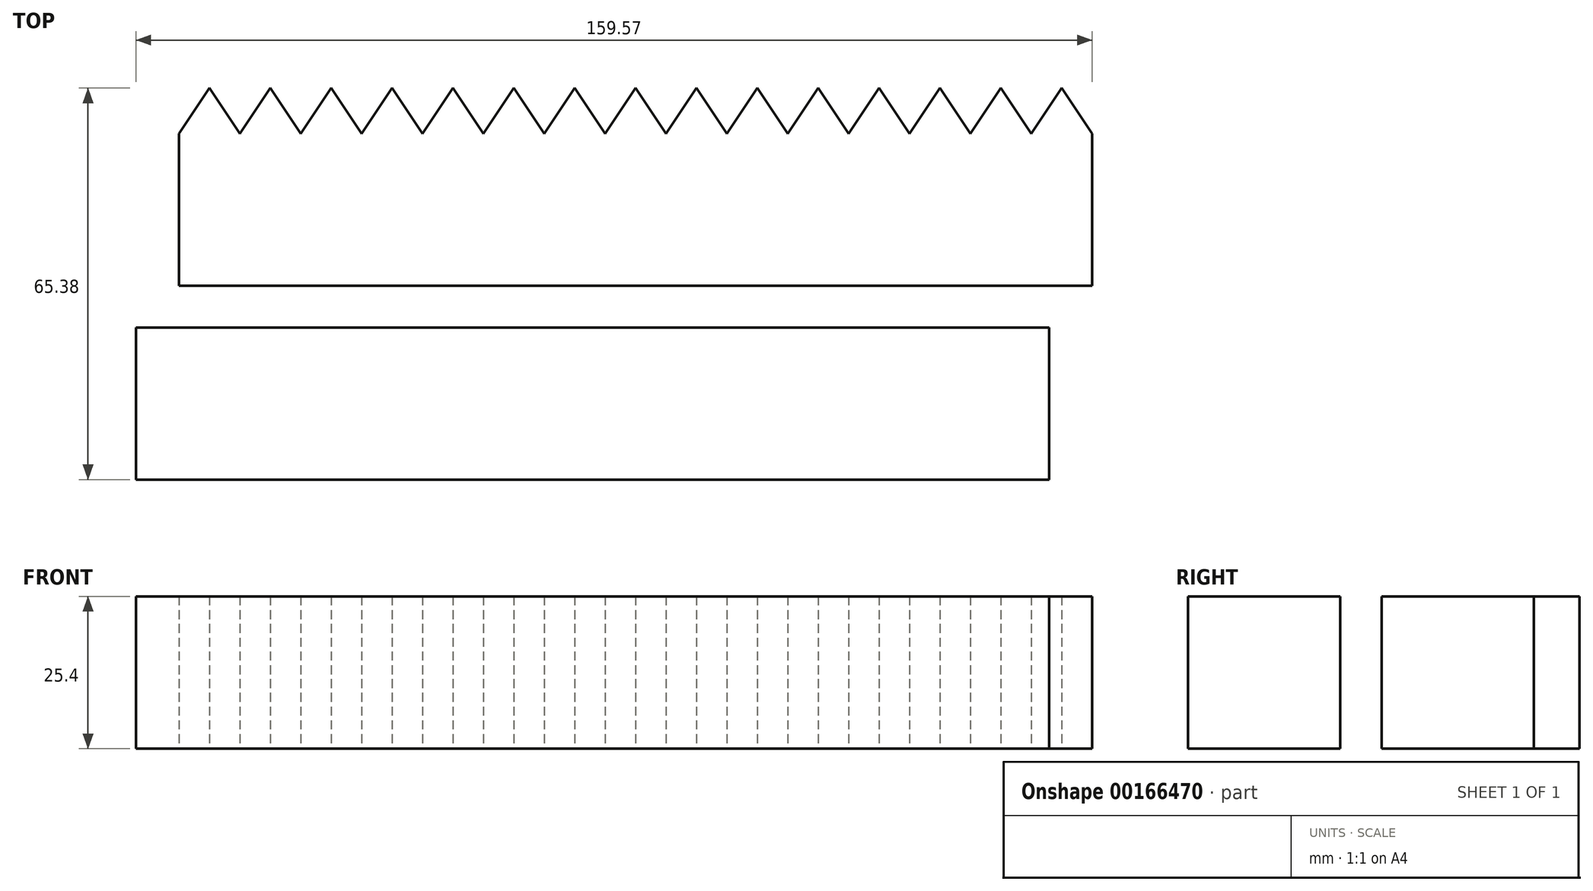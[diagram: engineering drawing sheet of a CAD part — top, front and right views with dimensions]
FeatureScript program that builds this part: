
annotation { "Feature Type Name" : "Feature", "Feature Type Description" : "" }
export const myFeature = defineFeature(function(context is Context, id is Id, definition is map)
    precondition{}
    {
        {
            var Q0;
            Q0=qCreatedBy(makeId("Top.planeOp"),FACE);
            var sketch = newSketch(context, id + "F0", { "sketchPlane" : qUnion([Q0])});
            skLineSegment(sketch, "E0.bottom", {"start": v(56.68, 12.19) * mm, "end": v(-95.72, 12.19) * mm});
            skLineSegment(sketch, "E0.top", {"start": v(56.68, -13.21) * mm, "end": v(-95.72, -13.21) * mm});
            skLineSegment(sketch, "E0.left", {"start": v(56.68, 12.19) * mm, "end": v(56.68, -13.21) * mm});
            skLineSegment(sketch, "E0.right", {"start": v(-95.72, 12.19) * mm, "end": v(-95.72, -13.21) * mm});
            skPoint(sketch, "E0.middle", {"position": v(-19.52, -0.51) * mm});
            skLineSegment(sketch, "E1", {"start": v(-90.64, 12.19) * mm, "end": v(-90.64, 19.8) * mm});
            skLineSegment(sketch, "E2", {"start": v(-90.64, 19.8) * mm, "end": v(-85.56, 12.19) * mm});
            skLineSegment(sketch, "E3", {"start": v(-85.56, 12.19) * mm, "end": v(-90.64, 19.8) * mm});
            skLineSegment(sketch, "E4", {"start": v(-95.72, 12.19) * mm, "end": v(-90.64, 19.8) * mm});
            skLineSegment(sketch, "E5.2.0.0", {"start": v(209.08, 12.19) * mm, "end": v(214.16, 19.8) * mm});
            skLineSegment(sketch, "E5.2.0.1", {"start": v(219.24, 12.19) * mm, "end": v(214.16, 19.8) * mm});
            skLineSegment(sketch, "E5.3.0.0", {"start": v(361.48, 12.19) * mm, "end": v(366.56, 19.8) * mm});
            skLineSegment(sketch, "E5.3.0.1", {"start": v(371.64, 12.19) * mm, "end": v(366.56, 19.8) * mm});
            skLineSegment(sketch, "E5.4.0.0", {"start": v(513.88, 12.19) * mm, "end": v(518.96, 19.8) * mm});
            skLineSegment(sketch, "E5.4.0.1", {"start": v(524.04, 12.19) * mm, "end": v(518.96, 19.8) * mm});
            skLineSegment(sketch, "E5.5.0.0", {"start": v(666.28, 12.19) * mm, "end": v(671.36, 19.8) * mm});
            skLineSegment(sketch, "E5.5.0.1", {"start": v(676.44, 12.19) * mm, "end": v(671.36, 19.8) * mm});
            skLineSegment(sketch, "E5.6.0.0", {"start": v(818.68, 12.19) * mm, "end": v(823.76, 19.8) * mm});
            skLineSegment(sketch, "E5.6.0.1", {"start": v(828.84, 12.19) * mm, "end": v(823.76, 19.8) * mm});
            skLineSegment(sketch, "E5.7.0.0", {"start": v(971.08, 12.19) * mm, "end": v(976.16, 19.8) * mm});
            skLineSegment(sketch, "E5.7.0.1", {"start": v(981.24, 12.19) * mm, "end": v(976.16, 19.8) * mm});
            skLineSegment(sketch, "E5.8.0.0", {"start": v(1123.48, 12.19) * mm, "end": v(1128.56, 19.8) * mm});
            skLineSegment(sketch, "E5.8.0.1", {"start": v(1133.64, 12.19) * mm, "end": v(1128.56, 19.8) * mm});
            skLineSegment(sketch, "E5.9.0.0", {"start": v(1275.88, 12.19) * mm, "end": v(1280.96, 19.8) * mm});
            skLineSegment(sketch, "E5.9.0.1", {"start": v(1286.04, 12.19) * mm, "end": v(1280.96, 19.8) * mm});
            skLineSegment(sketch, "E5.10.0.0", {"start": v(1428.28, 12.19) * mm, "end": v(1433.36, 19.8) * mm});
            skLineSegment(sketch, "E5.10.0.1", {"start": v(1438.44, 12.19) * mm, "end": v(1433.36, 19.8) * mm});
            skLineSegment(sketch, "E5.11.0.0", {"start": v(1580.68, 12.19) * mm, "end": v(1585.76, 19.8) * mm});
            skLineSegment(sketch, "E5.11.0.1", {"start": v(1590.84, 12.19) * mm, "end": v(1585.76, 19.8) * mm});
            skLineSegment(sketch, "E5.12.0.0", {"start": v(1733.08, 12.19) * mm, "end": v(1738.16, 19.8) * mm});
            skLineSegment(sketch, "E5.12.0.1", {"start": v(1743.24, 12.19) * mm, "end": v(1738.16, 19.8) * mm});
            skLineSegment(sketch, "E5.13.0.0", {"start": v(1885.48, 12.19) * mm, "end": v(1890.56, 19.8) * mm});
            skLineSegment(sketch, "E5.13.0.1", {"start": v(1895.64, 12.19) * mm, "end": v(1890.56, 19.8) * mm});
            skLineSegment(sketch, "E5.14.0.0", {"start": v(2037.88, 12.19) * mm, "end": v(2042.96, 19.8) * mm});
            skLineSegment(sketch, "E5.14.0.1", {"start": v(2048.04, 12.19) * mm, "end": v(2042.96, 19.8) * mm});
            skLineSegment(sketch, "E5.direction1", {"start": v(-95.72, 12.19) * mm, "end": v(56.68, 12.19) * mm, "construction": true});
            skLineSegment(sketch, "E6.1.0.0", {"start": v(-85.56, 12.19) * mm, "end": v(-80.48, 19.8) * mm});
            skLineSegment(sketch, "E6.1.0.1", {"start": v(-75.4, 12.19) * mm, "end": v(-80.48, 19.8) * mm});
            skLineSegment(sketch, "E6.2.0.0", {"start": v(-75.4, 12.19) * mm, "end": v(-70.32, 19.8) * mm});
            skLineSegment(sketch, "E6.2.0.1", {"start": v(-65.24, 12.19) * mm, "end": v(-70.32, 19.8) * mm});
            skLineSegment(sketch, "E6.3.0.0", {"start": v(-65.24, 12.19) * mm, "end": v(-60.16, 19.8) * mm});
            skLineSegment(sketch, "E6.3.0.1", {"start": v(-55.08, 12.19) * mm, "end": v(-60.16, 19.8) * mm});
            skLineSegment(sketch, "E6.4.0.0", {"start": v(-55.08, 12.19) * mm, "end": v(-50, 19.8) * mm});
            skLineSegment(sketch, "E6.4.0.1", {"start": v(-44.92, 12.19) * mm, "end": v(-50, 19.8) * mm});
            skLineSegment(sketch, "E6.5.0.0", {"start": v(-44.92, 12.19) * mm, "end": v(-39.84, 19.8) * mm});
            skLineSegment(sketch, "E6.5.0.1", {"start": v(-34.76, 12.19) * mm, "end": v(-39.84, 19.8) * mm});
            skLineSegment(sketch, "E6.6.0.0", {"start": v(-34.76, 12.19) * mm, "end": v(-29.68, 19.8) * mm});
            skLineSegment(sketch, "E6.6.0.1", {"start": v(-24.6, 12.19) * mm, "end": v(-29.68, 19.8) * mm});
            skLineSegment(sketch, "E6.7.0.0", {"start": v(-24.6, 12.19) * mm, "end": v(-19.52, 19.8) * mm});
            skLineSegment(sketch, "E6.7.0.1", {"start": v(-14.44, 12.19) * mm, "end": v(-19.52, 19.8) * mm});
            skLineSegment(sketch, "E6.8.0.0", {"start": v(-14.44, 12.19) * mm, "end": v(-9.36, 19.8) * mm});
            skLineSegment(sketch, "E6.8.0.1", {"start": v(-4.28, 12.19) * mm, "end": v(-9.36, 19.8) * mm});
            skLineSegment(sketch, "E6.9.0.0", {"start": v(-4.28, 12.19) * mm, "end": v(0.8, 19.8) * mm});
            skLineSegment(sketch, "E6.9.0.1", {"start": v(5.88, 12.19) * mm, "end": v(0.8, 19.8) * mm});
            skLineSegment(sketch, "E6.10.0.0", {"start": v(5.88, 12.19) * mm, "end": v(10.96, 19.8) * mm});
            skLineSegment(sketch, "E6.10.0.1", {"start": v(16.04, 12.19) * mm, "end": v(10.96, 19.8) * mm});
            skLineSegment(sketch, "E6.11.0.0", {"start": v(16.04, 12.19) * mm, "end": v(21.12, 19.8) * mm});
            skLineSegment(sketch, "E6.11.0.1", {"start": v(26.2, 12.19) * mm, "end": v(21.12, 19.8) * mm});
            skLineSegment(sketch, "E6.12.0.0", {"start": v(26.2, 12.19) * mm, "end": v(31.28, 19.8) * mm});
            skLineSegment(sketch, "E6.12.0.1", {"start": v(36.36, 12.19) * mm, "end": v(31.28, 19.8) * mm});
            skLineSegment(sketch, "E6.13.0.0", {"start": v(36.36, 12.19) * mm, "end": v(41.44, 19.8) * mm});
            skLineSegment(sketch, "E6.13.0.1", {"start": v(46.52, 12.19) * mm, "end": v(41.44, 19.8) * mm});
            skLineSegment(sketch, "E6.14.0.0", {"start": v(46.52, 12.19) * mm, "end": v(51.6, 19.8) * mm});
            skLineSegment(sketch, "E6.14.0.1", {"start": v(56.68, 12.19) * mm, "end": v(51.6, 19.8) * mm});
            skLineSegment(sketch, "E6.direction1", {"start": v(-95.72, 12.19) * mm, "end": v(-85.56, 12.19) * mm, "construction": true});
            skSolve(sketch);
        }
        {
            var Q0;
            {var subQ0=sQuery(id+"F0.wireOp",EDGE,"E1");Q0=makeQuery(id+"F0.imprint","IMPRINT",FACE,{"disambiguationData":[TD([[makeQuery(id+"F0.imprint","IMPRINT",EDGE,{"derivedFrom":subQ0}),-1.0]])]});}
            var Q1;
            {var subQ2=sQuery(id+"F0.wireOp",EDGE,"E1");Q1=makeQuery(id+"F0.imprint","IMPRINT",FACE,{"disambiguationData":[TD([[makeQuery(id+"F0.imprint","IMPRINT",EDGE,{"derivedFrom":subQ2}),1.0]])]});}
            var Q2;
            {var subQ0=sQuery(id+"F0.wireOp",EDGE,"E6.1.0.0");Q2=makeQuery(id+"F0.imprint","IMPRINT",FACE,{"disambiguationData":[TD([[makeQuery(id+"F0.imprint","IMPRINT",EDGE,{"derivedFrom":subQ0}),-1.0]])]});}
            var Q3;
            {var subQ0=sQuery(id+"F0.wireOp",EDGE,"E6.2.0.0");Q3=makeQuery(id+"F0.imprint","IMPRINT",FACE,{"disambiguationData":[TD([[makeQuery(id+"F0.imprint","IMPRINT",EDGE,{"derivedFrom":subQ0}),-1.0]])]});}
            var Q4;
            {var subQ0=sQuery(id+"F0.wireOp",EDGE,"E6.3.0.0");Q4=makeQuery(id+"F0.imprint","IMPRINT",FACE,{"disambiguationData":[TD([[makeQuery(id+"F0.imprint","IMPRINT",EDGE,{"derivedFrom":subQ0}),-1.0]])]});}
            var Q5;
            {var subQ0=sQuery(id+"F0.wireOp",EDGE,"E6.4.0.0");Q5=makeQuery(id+"F0.imprint","IMPRINT",FACE,{"disambiguationData":[TD([[makeQuery(id+"F0.imprint","IMPRINT",EDGE,{"derivedFrom":subQ0}),-1.0]])]});}
            var Q6;
            {var subQ0=sQuery(id+"F0.wireOp",EDGE,"E6.5.0.0");Q6=makeQuery(id+"F0.imprint","IMPRINT",FACE,{"disambiguationData":[TD([[makeQuery(id+"F0.imprint","IMPRINT",EDGE,{"derivedFrom":subQ0}),-1.0]])]});}
            var Q7;
            {var subQ0=sQuery(id+"F0.wireOp",EDGE,"E6.6.0.0");Q7=makeQuery(id+"F0.imprint","IMPRINT",FACE,{"disambiguationData":[TD([[makeQuery(id+"F0.imprint","IMPRINT",EDGE,{"derivedFrom":subQ0}),-1.0]])]});}
            var Q8;
            {var subQ0=sQuery(id+"F0.wireOp",EDGE,"E6.7.0.0");Q8=makeQuery(id+"F0.imprint","IMPRINT",FACE,{"disambiguationData":[TD([[makeQuery(id+"F0.imprint","IMPRINT",EDGE,{"derivedFrom":subQ0}),-1.0]])]});}
            var Q9;
            {var subQ0=sQuery(id+"F0.wireOp",EDGE,"E6.8.0.0");Q9=makeQuery(id+"F0.imprint","IMPRINT",FACE,{"disambiguationData":[TD([[makeQuery(id+"F0.imprint","IMPRINT",EDGE,{"derivedFrom":subQ0}),-1.0]])]});}
            var Q10;
            {var subQ0=sQuery(id+"F0.wireOp",EDGE,"E6.9.0.0");Q10=makeQuery(id+"F0.imprint","IMPRINT",FACE,{"disambiguationData":[TD([[makeQuery(id+"F0.imprint","IMPRINT",EDGE,{"derivedFrom":subQ0}),-1.0]])]});}
            var Q11;
            {var subQ0=sQuery(id+"F0.wireOp",EDGE,"E6.10.0.0");Q11=makeQuery(id+"F0.imprint","IMPRINT",FACE,{"disambiguationData":[TD([[makeQuery(id+"F0.imprint","IMPRINT",EDGE,{"derivedFrom":subQ0}),-1.0]])]});}
            var Q12;
            {var subQ0=sQuery(id+"F0.wireOp",EDGE,"E6.11.0.0");Q12=makeQuery(id+"F0.imprint","IMPRINT",FACE,{"disambiguationData":[TD([[makeQuery(id+"F0.imprint","IMPRINT",EDGE,{"derivedFrom":subQ0}),-1.0]])]});}
            var Q13;
            {var subQ0=sQuery(id+"F0.wireOp",EDGE,"E6.12.0.0");Q13=makeQuery(id+"F0.imprint","IMPRINT",FACE,{"disambiguationData":[TD([[makeQuery(id+"F0.imprint","IMPRINT",EDGE,{"derivedFrom":subQ0}),-1.0]])]});}
            var Q14;
            {var subQ0=sQuery(id+"F0.wireOp",EDGE,"E6.13.0.0");Q14=makeQuery(id+"F0.imprint","IMPRINT",FACE,{"disambiguationData":[TD([[makeQuery(id+"F0.imprint","IMPRINT",EDGE,{"derivedFrom":subQ0}),-1.0]])]});}
            var Q15;
            {var subQ2=sQuery(id+"F0.wireOp",EDGE,"E6.14.0.0");Q15=makeQuery(id+"F0.imprint","IMPRINT",FACE,{"disambiguationData":[TD([[makeQuery(id+"F0.imprint","IMPRINT",EDGE,{"derivedFrom":subQ2}),-1.0]])]});}
            var Q16;
            Q16=makeQuery(id+"F0.imprint","IMPRINT",FACE,{"disambiguationData":[TD([[makeQuery(id+"F0.imprint","IMPRINT",EDGE,{"derivedFrom":sQuery(id+"F0.wireOp",EDGE,"E0.top")}),-1.0]])]});
            extrude(context, id + "F1", {"entities" : qUnion([Q0, Q1, Q2, Q3, Q4, Q5, Q6, Q7, Q8, Q9, Q10, Q11, Q12, Q13, Q14, Q15, Q16]), "depth" : 25.4 * mm});
        }
        {
            var Q0;
            Q0=qCreatedBy(makeId("Top.planeOp"),FACE);
            var sketch = newSketch(context, id + "F2", { "sketchPlane" : qUnion([Q0])});
            skLineSegment(sketch, "E7.bottom", {"start": v(49.5, -45.57) * mm, "end": v(-102.9, -45.57) * mm});
            skLineSegment(sketch, "E7.top", {"start": v(49.5, -20.17) * mm, "end": v(-102.9, -20.17) * mm});
            skLineSegment(sketch, "E7.left", {"start": v(49.5, -45.57) * mm, "end": v(49.5, -20.17) * mm});
            skLineSegment(sketch, "E7.right", {"start": v(-102.9, -45.57) * mm, "end": v(-102.9, -20.17) * mm});
            skPoint(sketch, "E7.middle", {"position": v(-26.7, -32.87) * mm});
            skSolve(sketch);
        }
        {
            var Q0;
            Q0=makeQuery(id+"F2.imprint","IMPRINT",FACE,{"disambiguationData":[TD([[makeQuery(id+"F2.imprint","IMPRINT",EDGE,{"derivedFrom":sQuery(id+"F2.wireOp",EDGE,"E7.bottom")}),-1.0]])]});
            extrude(context, id + "F3", {"entities" : qUnion([Q0]), "depth" : 25.4 * mm});
        }
    });
